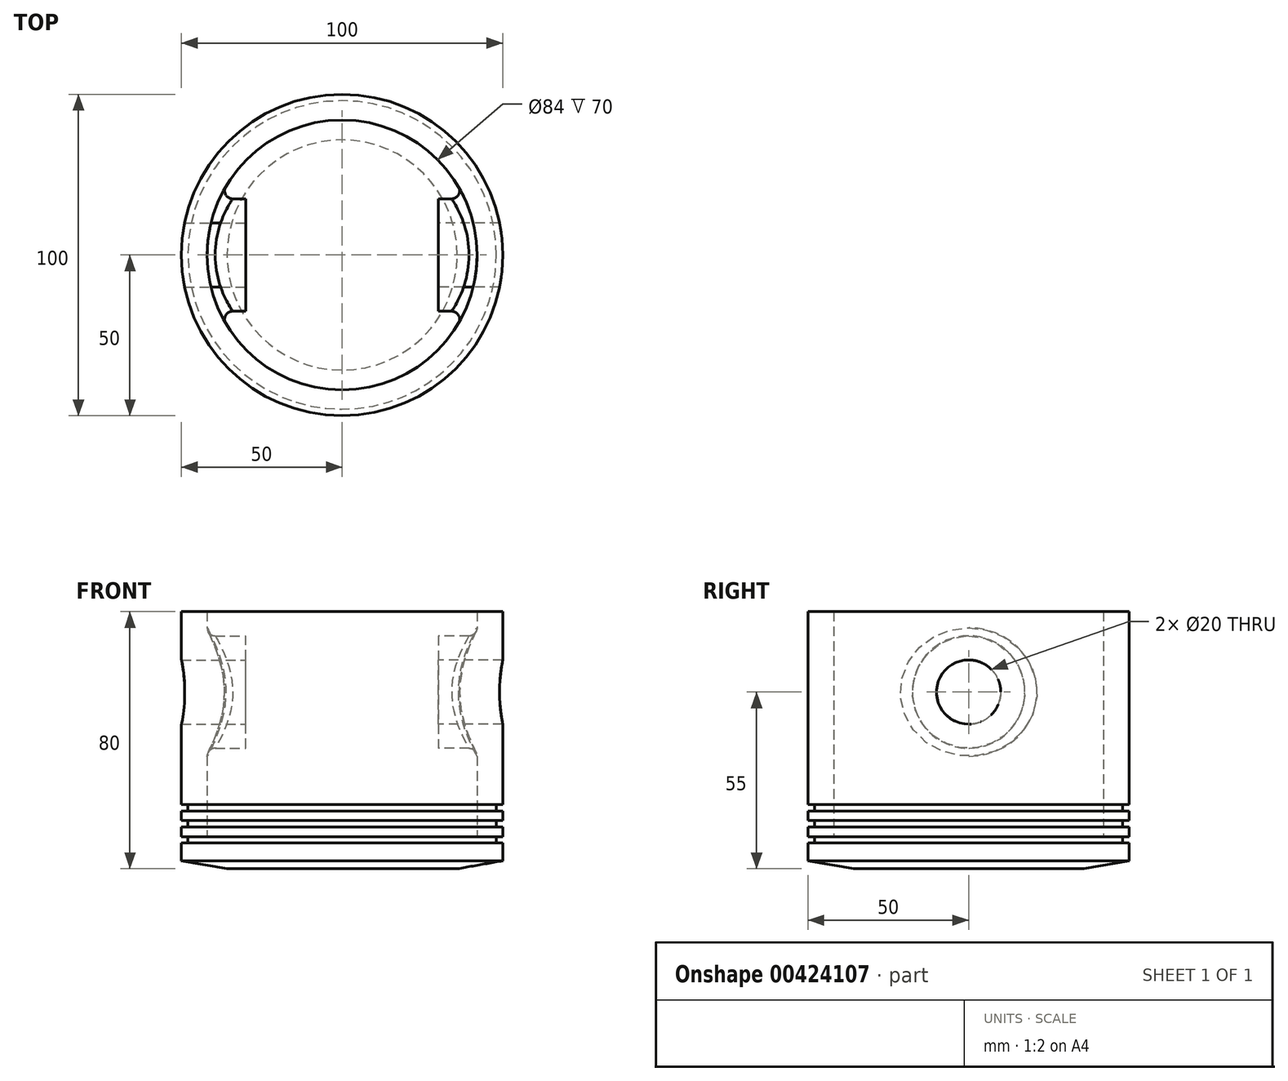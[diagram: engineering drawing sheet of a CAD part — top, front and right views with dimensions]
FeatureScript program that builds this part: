
annotation { "Feature Type Name" : "Feature", "Feature Type Description" : "" }
export const myFeature = defineFeature(function(context is Context, id is Id, definition is map)
    precondition{}
    {
        {
            var Q0;
            Q0=qCreatedBy(makeId("Top.planeOp"),FACE);
            var sketch = newSketch(context, id + "F0", { "sketchPlane" : qUnion([Q0])});
            skCircle(sketch, "E0", {"center": v(0, 0) * mm, "radius": 50 * mm});
            skCircle(sketch, "E1.0", {"center": v(0, 0) * mm, "radius": 42 * mm});
            skCircle(sketch, "E2.0", {"center": v(0, 0) * mm, "radius": 48 * mm});
            skSolve(sketch);
        }
        {
            var Q0;
            Q0=makeQuery(id+"F0.imprint","IMPRINT",FACE,{"disambiguationData":[TD([[makeQuery(id+"F0.imprint","IMPRINT",EDGE,{"derivedFrom":sQuery(id+"F0.wireOp",EDGE,"E0")}),1.0]])]});
            var Q1;
            Q1=makeQuery(id+"F0.imprint","IMPRINT",FACE,{"disambiguationData":[TD([[makeQuery(id+"F0.imprint","IMPRINT",EDGE,{"derivedFrom":sQuery(id+"F0.wireOp",EDGE,"E1.0")}),-1.0]])]});
            var Q2;
            Q2=makeQuery(id+"F0.imprint","IMPRINT",FACE,{"disambiguationData":[TD([[makeQuery(id+"F0.imprint","IMPRINT",EDGE,{"derivedFrom":sQuery(id+"F0.wireOp",EDGE,"E1.0")}),1.0]])]});
            extrude(context, id + "F1", {"entities" : qUnion([Q0, Q1, Q2]), "oppositeDirection" : true, "depth" : 10 * mm});
        }
        {
            var Q0;
            Q0=makeQuery(id+"F0.imprint","IMPRINT",FACE,{"disambiguationData":[TD([[makeQuery(id+"F0.imprint","IMPRINT",EDGE,{"derivedFrom":sQuery(id+"F0.wireOp",EDGE,"E1.0")}),-1.0]])]});
            var Q1;
            Q1=makeQuery(id+"F0.imprint","IMPRINT",FACE,{"disambiguationData":[TD([[makeQuery(id+"F0.imprint","IMPRINT",EDGE,{"derivedFrom":sQuery(id+"F0.wireOp",EDGE,"E0")}),1.0]])]});
            extrude(context, id + "F2", {"entities" : qUnion([Q0, Q1]), "operationType" : NewBodyOperationType.ADD, "depth" : 70 * mm});
        }
        {
            var Q0;
            Q0=makeQuery(id+"F0.imprint","IMPRINT",FACE,{"disambiguationData":[TD([[makeQuery(id+"F0.imprint","IMPRINT",EDGE,{"derivedFrom":sQuery(id+"F0.wireOp",EDGE,"E0")}),1.0]])]});
            extrude(context, id + "F3", {"entities" : qUnion([Q0]), "operationType" : NewBodyOperationType.REMOVE, "oppositeDirection" : true, "depth" : 2 * mm});
        }
        {
            var Q0;
            Q0=makeQuery(id+"F0.imprint","IMPRINT",FACE,{"disambiguationData":[TD([[makeQuery(id+"F0.imprint","IMPRINT",EDGE,{"derivedFrom":sQuery(id+"F0.wireOp",EDGE,"E0")}),1.0]])]});
            extrude(context, id + "F4", {"entities" : qUnion([Q0]), "operationType" : NewBodyOperationType.REMOVE, "depth" : 5 * mm, "hasSecondDirection" : true, "secondDirectionOppositeDirection" : false, "secondDirectionDepth" : 3 * mm});
        }
        {
            var Q0;
            Q0=qSketchRegion(id+"F0",true);
            extrude(context, id + "F5", {"entities" : qUnion([Q0]), "operationType" : NewBodyOperationType.REMOVE, "depth" : 10 * mm, "hasSecondDirection" : true, "secondDirectionOppositeDirection" : false, "secondDirectionDepth" : 8 * mm});
        }
        {
            var Q0;
            Q0=makeQuery(id+"F1.opExtrude","CAP_EDGE",EDGE,{"disambiguationData":[OSD([sQuery(id+"F0.wireOp",EDGE,"E0")])],"isStart":false});
            chamfer(context, id + "F6", {"entities" : qUnion([Q0]), "chamferType" : ChamferType.OFFSET_ANGLE, "width" : 2.5 * mm, "oppositeDirection" : false, "angle" : 80 * degree, "tangentPropagation" : true});
        }
        {
            var Q0;
            Q0=qCreatedBy(makeId("Right.planeOp"),FACE);
            var sketch = newSketch(context, id + "F7", { "sketchPlane" : qUnion([Q0])});
            skCircle(sketch, "E3", {"center": v(0, 45) * mm, "radius": 10 * mm});
            skCircle(sketch, "E4", {"center": v(0, 45) * mm, "radius": 17.5 * mm});
            skSolve(sketch);
        }
        {
            var Q0;
            Q0=makeQuery(id+"F7.imprint","IMPRINT",FACE,{"disambiguationData":[TD([[makeQuery(id+"F7.imprint","IMPRINT",EDGE,{"derivedFrom":sQuery(id+"F7.wireOp",EDGE,"E3")}),-1.0]])]});
            extrude(context, id + "F8", {"entities" : qUnion([Q0]), "operationType" : NewBodyOperationType.ADD, "depth" : 45 * mm, "hasSecondDirection" : true, "secondDirectionOppositeDirection" : false, "secondDirectionDepth" : 30 * mm});
        }
        {
            var Q0;
            Q0=qSketchRegion(id+"F7",true);
            extrude(context, id + "F9", {"entities" : qUnion([Q0]), "operationType" : NewBodyOperationType.ADD, "oppositeDirection" : true, "depth" : 45 * mm, "hasSecondDirection" : true, "secondDirectionOppositeDirection" : true, "secondDirectionDepth" : 30 * mm});
        }
        {
            var Q0;
            Q0=makeQuery(id+"F7.imprint","IMPRINT",FACE,{"disambiguationData":[TD([[makeQuery(id+"F7.imprint","IMPRINT",EDGE,{"derivedFrom":sQuery(id+"F7.wireOp",EDGE,"E3")}),1.0]])]});
            extrude(context, id + "F10", {"entities" : qUnion([Q0]), "operationType" : NewBodyOperationType.REMOVE, "endBound" : BoundingType.THROUGH_ALL, "oppositeDirection" : true, "depth" : 25 * mm, "hasSecondDirection" : true, "secondDirectionBound" : SecondDirectionBoundingType.THROUGH_ALL, "secondDirectionOppositeDirection" : false, "secondDirectionDepth" : 25 * mm});
        }
        {
            var Q0;
            Q0=makeQuery(id+"F2.opExtrude","CAP_EDGE",EDGE,{"disambiguationData":[OSD([sQuery(id+"F0.wireOp",EDGE,"E1.0")])],"isStart":true});
            var Q1;
            Q1=makeQuery(id+"F8.boolean.opBoolean","INTERSECT",EDGE,{"derivedFrom":[makeQuery(id+"F2.opExtrude","SWEPT_FACE",FACE,{"disambiguationData":[OSD([sQuery(id+"F0.wireOp",EDGE,"E1.0")])]}),makeQuery(id+"F8.opExtrude","SWEPT_FACE",FACE,{"disambiguationData":[OSD([sQuery(id+"F7.wireOp",EDGE,"E4")])]})]});
            var Q2;
            {var subQ0=sQuery(id+"F7.wireOp",EDGE,"E4");var subQ1=sQuery(id+"F0.wireOp",EDGE,"E0");var subQ2=sQuery(id+"F0.wireOp",EDGE,"E1.0");Q2=makeQuery(id+"F9.boolean.opBoolean","INTERSECT",EDGE,{"derivedFrom":[makeQuery(id+"F8.boolean.opBoolean","SPLIT",FACE,{"disambiguationData":[TD([makeQuery(id+"F1.opExtrude","CAP_FACE",FACE,{"disambiguationData":[OSD([subQ1])],"isStart":true})])],"derivedFrom":makeQuery(id+"F2.opExtrude","SWEPT_FACE",FACE,{"disambiguationData":[OSD([subQ2])]})}),makeQuery(id+"F9.opExtrude","SWEPT_FACE",FACE,{"disambiguationData":[OSD([subQ0])]})]});}
            fillet(context, id + "F11", {"entities" : qUnion([Q0, Q1, Q2]), "radius" : 2.5 * mm, "tangentPropagation" : true, "allowEdgeOverflow" : false});
        }
    });
